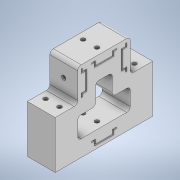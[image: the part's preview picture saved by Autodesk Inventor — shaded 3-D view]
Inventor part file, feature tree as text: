
AUTODESK INVENTOR PART (.ipt)
format: ipt  version: 2021 (Build 250183000, 183)  size: 274,432 bytes
history: native  units: mm
features: extrude x7, sketch x7, projected_geometry x4, fillet x2
ambient origin geometry x8: Origin, YZ Plane, XZ Plane, XY Plane, X Axis, Y Axis, Z Axis, Center Point
bodies: Solid1 (feature_tree)
feature tree (20):
  extrude  "Extrusion1"  Depth=40.0mm
  extrude  "Extrusion2"  Depth=4.0mm
  extrude  "Extrusion3"  Depth=5.7mm
  sketch  "Sketch4"  dims[d11=6.2mm d12=24.5mm]
  sketch  "Sketch5"  dims[d13=5.7mm d14=1.7mm]
  extrude  "Extrusion4"  Depth=24.5mm
  extrude  "Extrusion5"  Depth=1.7mm
  extrude  "Extrusion6"  Depth=6.0mm
  extrude  "Extrusion7"  Depth=5.0mm
  fillet  "Fillet1"  Radius=5.0mm
  fillet  "Fillet2"  Radius=68.5mm
  sketch  "Sketch1"  dims[d0=140.0mm d1=40.0mm]
  sketch  "Sketch2"  dims[d2=68.5mm d3=0.0mm d8=4.0mm]
  sketch  "Sketch3"  dims[d9=1.7mm d10=5.7mm]
  projected_geometry  "Projected Loop1"
  projected_geometry  "Projected Loop2"
  sketch  "Sketch6"  dims[d15=4.0mm d16=6.0mm]
  projected_geometry  "Projected Loop3"
  projected_geometry  "Projected Loop4"
  sketch  "Sketch7"  dims[d17=5.0mm d18=5.0mm d19=5.0mm d20=68.5mm d21=0.0mm d27=6.0mm d31=6.0mm d33=10.0mm d34=0.0mm d37=6.1mm d38=6.1mm d39=6.1mm d40=6.1mm d41=10.0mm d42=0.0mm d43=10.0mm d44=0.0mm d45=10.0mm d46=0.0mm d48=6.1mm d49=6.1mm d52=6.0mm d53=12.0mm d54=10.0mm d55=0.0mm d58=40.0mm d59=6.0mm d60=5.0mm d61=10.0mm d62=5.0mm]
